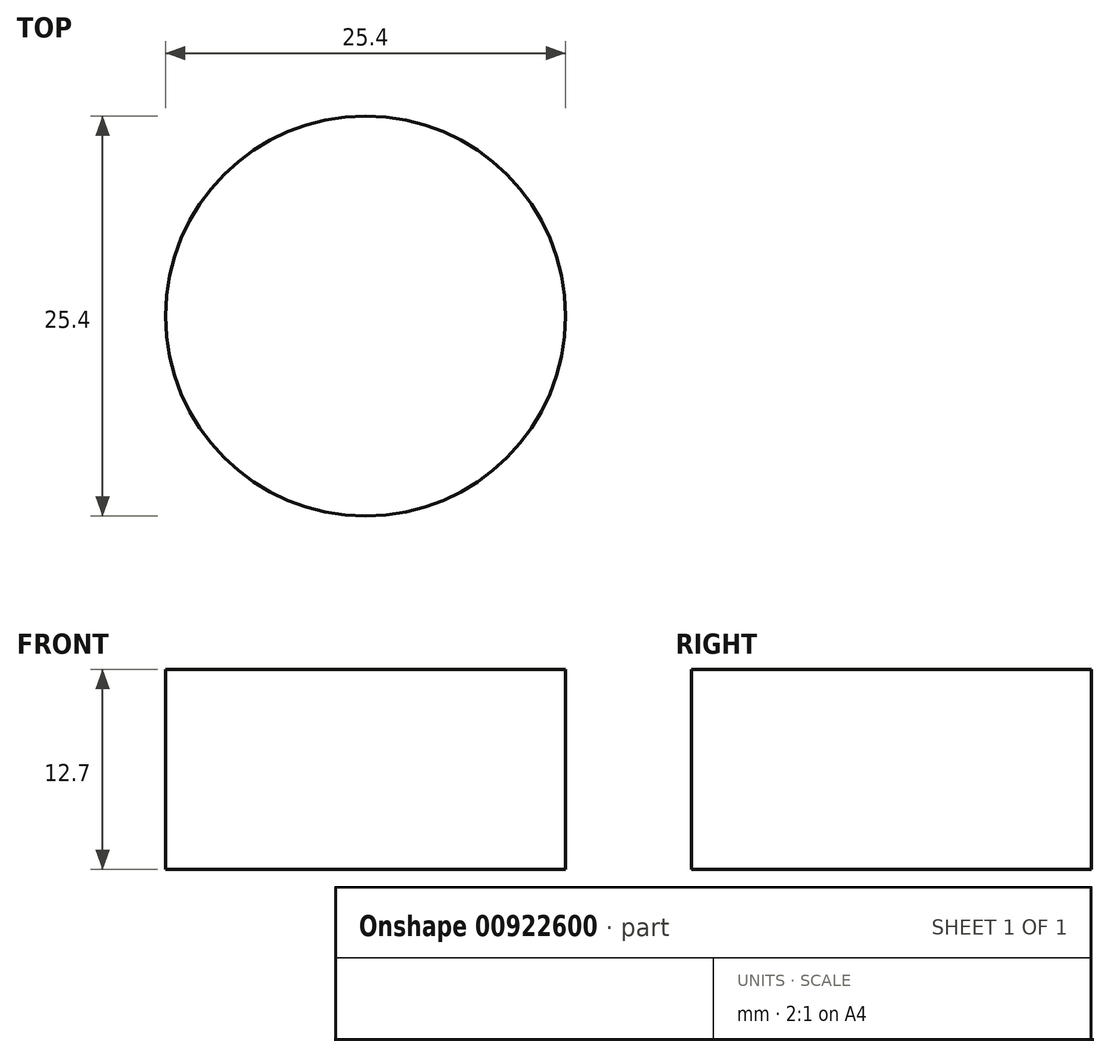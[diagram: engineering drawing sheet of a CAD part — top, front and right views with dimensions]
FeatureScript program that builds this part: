
annotation { "Feature Type Name" : "Feature", "Feature Type Description" : "" }
export const myFeature = defineFeature(function(context is Context, id is Id, definition is map)
    precondition{}
    {
        {
            var Q0;
            Q0=qCreatedBy(makeId("Top.planeOp"),FACE);
            var sketch = newSketch(context, id + "F0", { "sketchPlane" : qUnion([Q0])});
            skCircle(sketch, "E0", {"center": v(0, 0) * mm, "radius": 12.7 * mm});
            skSolve(sketch);
        }
        {
            var Q0;
            Q0 = qSketchRegion(id + "F0", true);
            extrude(context, id + "F1", {"entities" : qUnion([Q0]), "depth" : 12.7 * mm, "offsetDistance" : 25.4 * mm});
        }
    });
